# Revit family: Access_Door-Acudor-Non-Rated_Flush-PA-3000_Series
name_source: partatom
category: Specialty Equipment
revit_build: Autodesk Revit 2014 (Build: 20130308_1515(x64)
units: mm (PartAtom-declared; Revit-internal decimal feet)

## types (9) — shared parameters
Assembly Code = C1020700
Ceiling Mounted = Yes
Default Elevation = 48"
Description = Flush Non-Rated Plastic Access Door
Finish = Styrene Plastic-Acudor-Powder White
Installation Type = Ceiling Mounted
Length = 13/16"
Manufacturer = Acudor
Material = Styrene Plastic-Acudor-Powder White
Product Documentation Link = https://acudor.com
Product Page URL = https://acudor.com
URL = http://acudor.com
Wall Mounted = No

## per-type parameters (varying)
| type | Height | Width |
| PA-3000 4x6 | 6" | 4" |
| PA-3000 6x9 | 9" | 6" |
| PA-3000 8x8 | 8" | 8" |
| PA-3000 12x12 | 12" | 12" |
| PA-3000 14x14 | 14" | 14" |
| PA-3000 14x29 | 29" | 14" |
| PA-3000 18x18 | 18" | 18" |
| PA-3000 22x22 | 22" | 22" |
| PA-3000 24x24 | 24" | 24" |

note: column(s) folded — value = type name in every type: Model

## geometry (parser evidence)
native form markers: Sweep x1
no freeform markers — native parametric forms only
